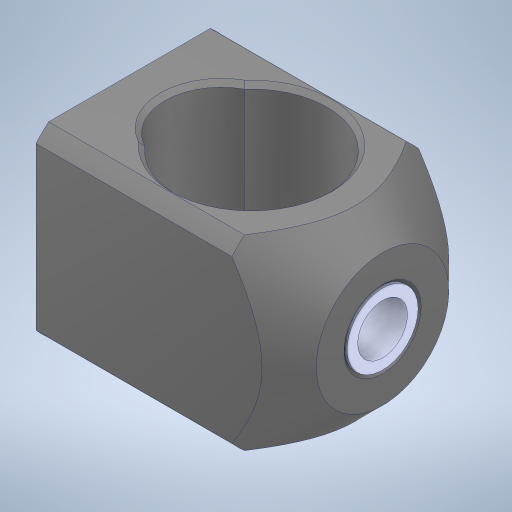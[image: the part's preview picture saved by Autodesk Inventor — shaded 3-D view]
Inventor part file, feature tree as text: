
AUTODESK INVENTOR PART (.ipt)
format: ipt  version: 2023 (Build 270158000, 158)  size: 294,912 bytes
history: mixed  units: in
note: dims shown in document units (in); Inventor stores cm internally (conversion verified against a paired STEP export)
features: extrude x3, sketch x3, other x1, imported_body x1
ambient origin geometry x8: Origin, YZ Plane, XZ Plane, XY Plane, X Axis, Y Axis, Z Axis, Center Point
bodies: Solid1 (imported_parasolid)
feature tree (8):
  other  "6669-001-1-solid1"
  extrude  "Extrusion1"  Depth=0.3937in
  sketch  "Sketch2"  dims[d3=0.3937in d4=0.0in d5=0.0in d6=0.0in]
  extrude  "Extrusion2"  TaperAngle=0.0deg  [1 undecoded]
  extrude  "Extrusion3"  [1 undecoded]
  sketch  "Sketch1"  dims[d0=0.3937in d1=0.0in d2=0.1654in]
  sketch  "Sketch3"
  imported_body  NMx_Import_Brep_tag  [imported B-rep: ~6 faces, bbox_mm=None]
note: 2 required parameter values undecoded (feature->parameter linkage not recoverable at this tier; creation-order binding heuristic only, values carry confidence <= 0.55)
